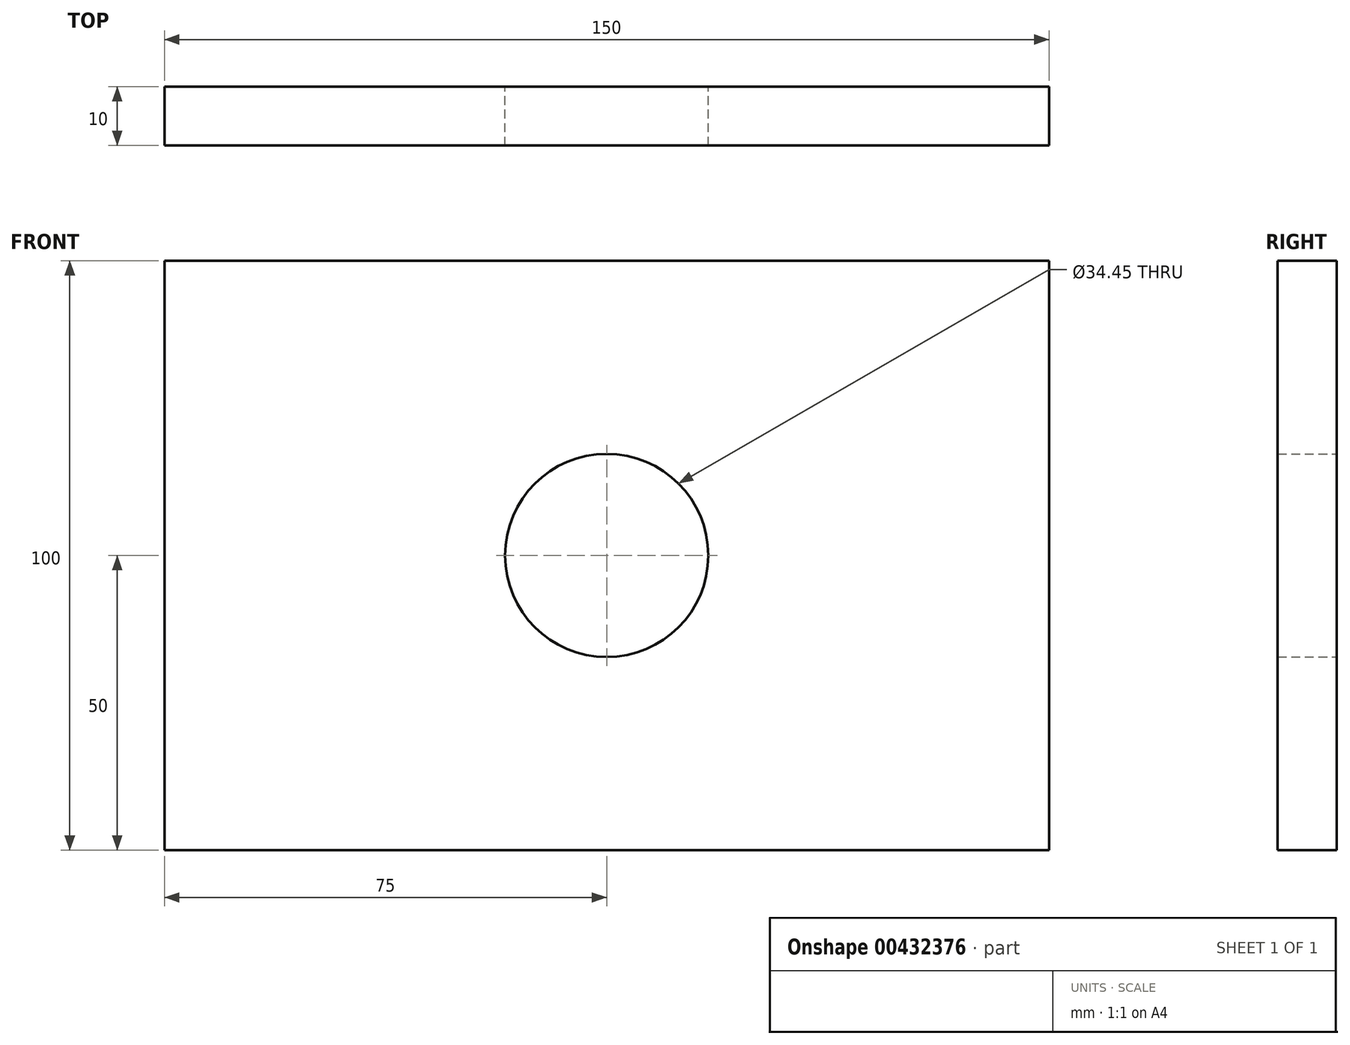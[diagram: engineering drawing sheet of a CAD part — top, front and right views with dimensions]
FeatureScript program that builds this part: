
annotation { "Feature Type Name" : "Feature", "Feature Type Description" : "" }
export const myFeature = defineFeature(function(context is Context, id is Id, definition is map)
    precondition{}
    {
        {
            var Q0;
            Q0=qCreatedBy(makeId("Front.planeOp"),FACE);
            var sketch = newSketch(context, id + "F0", { "sketchPlane" : qUnion([Q0])});
            skLineSegment(sketch, "E0.bottom", {"start": v(75, 50) * mm, "end": v(-75, 50) * mm});
            skLineSegment(sketch, "E0.top", {"start": v(75, -50) * mm, "end": v(-75, -50) * mm});
            skLineSegment(sketch, "E0.left", {"start": v(75, 50) * mm, "end": v(75, -50) * mm});
            skLineSegment(sketch, "E0.right", {"start": v(-75, 50) * mm, "end": v(-75, -50) * mm});
            skPoint(sketch, "E0.middle", {"position": v(0, 0) * mm});
            skCircle(sketch, "E1", {"center": v(0, 0) * mm, "radius": 17.23 * mm});
            skSolve(sketch);
        }
        {
            var Q0;
            Q0 = qSketchRegion(id + "F0", true);
            extrude(context, id + "F1", {"entities" : qUnion([Q0]), "endBound" : BoundingType.SYMMETRIC, "depth" : 10 * mm});
        }
    });
